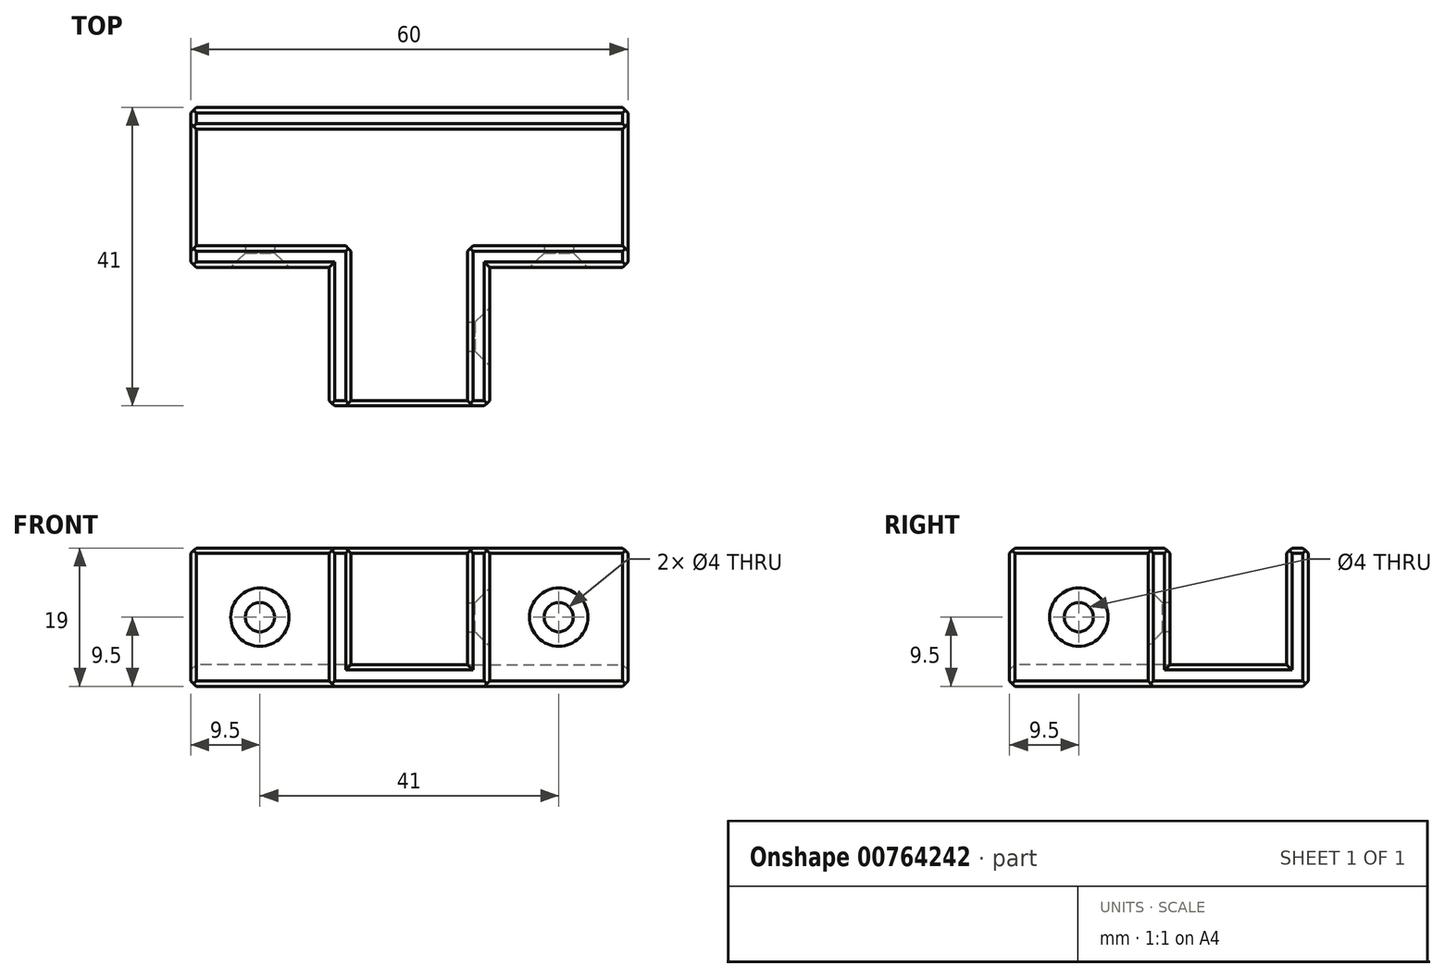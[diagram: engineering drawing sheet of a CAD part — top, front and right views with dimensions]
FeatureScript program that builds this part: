
annotation { "Feature Type Name" : "Feature", "Feature Type Description" : "" }
export const myFeature = defineFeature(function(context is Context, id is Id, definition is map)
    precondition{}
    {
        {
            var Q0;
            Q0=qCreatedBy(makeId("Top.planeOp"),FACE);
            var sketch = newSketch(context, id + "F0", { "sketchPlane" : qUnion([Q0])});
            skLineSegment(sketch, "E0.bottom", {"start": v(0, 0) * mm, "end": v(60, 0) * mm});
            skLineSegment(sketch, "E0.top", {"start": v(0, 22) * mm, "end": v(60, 22) * mm});
            skLineSegment(sketch, "E0.left", {"start": v(0, 0) * mm, "end": v(0, 22) * mm});
            skLineSegment(sketch, "E0.right", {"start": v(60, 0) * mm, "end": v(60, 22) * mm});
            skLineSegment(sketch, "E1", {"start": v(0, 0) * mm, "end": v(19, 0) * mm});
            skLineSegment(sketch, "E2.bottom", {"start": v(19, 0) * mm, "end": v(41, 0) * mm});
            skLineSegment(sketch, "E2.top", {"start": v(19, -19) * mm, "end": v(41, -19) * mm});
            skLineSegment(sketch, "E2.left", {"start": v(19, 0) * mm, "end": v(19, -19) * mm});
            skLineSegment(sketch, "E2.right", {"start": v(41, 0) * mm, "end": v(41, -19) * mm});
            skSolve(sketch);
        }
        {
            var Q0;
            Q0 = qSketchRegion(id + "F0", true);
            extrude(context, id + "F1", {"entities" : qUnion([Q0]), "depth" : 3 * mm, "offsetDistance" : 25 * mm});
        }
        {
            var Q0;
            Q0=makeQuery(id+"F1.opExtrude","CAP_FACE",FACE,{"disambiguationData":[OSD([sQuery(id+"F0.wireOp",EDGE,"E0.bottom"),sQuery(id+"F0.wireOp",EDGE,"E0.top"),sQuery(id+"F0.wireOp",EDGE,"E0.left"),sQuery(id+"F0.wireOp",EDGE,"E0.right"),sQuery(id+"F0.wireOp",EDGE,"E1"),sQuery(id+"F0.wireOp",EDGE,"E2.top"),sQuery(id+"F0.wireOp",EDGE,"E2.left"),sQuery(id+"F0.wireOp",EDGE,"E2.right")])],"isStart":false});
            var sketch = newSketch(context, id + "F2", { "sketchPlane" : qUnion([Q0])});
            skLineSegment(sketch, "E3.bottom", {"start": v(0, 22) * mm, "end": v(60, 22) * mm});
            skLineSegment(sketch, "E3.top", {"start": v(0, 19) * mm, "end": v(60, 19) * mm});
            skLineSegment(sketch, "E3.left", {"start": v(0, 22) * mm, "end": v(0, 19) * mm});
            skLineSegment(sketch, "E3.right", {"start": v(60, 22) * mm, "end": v(60, 19) * mm});
            skLineSegment(sketch, "E4.bottom", {"start": v(19, 0) * mm, "end": v(22, 0) * mm});
            skLineSegment(sketch, "E4.top", {"start": v(19, -19) * mm, "end": v(22, -19) * mm});
            skLineSegment(sketch, "E4.left", {"start": v(19, 0) * mm, "end": v(19, -19) * mm});
            skLineSegment(sketch, "E4.right", {"start": v(22, 0) * mm, "end": v(22, -19) * mm});
            skLineSegment(sketch, "E5.bottom", {"start": v(41, 0) * mm, "end": v(38, 0) * mm});
            skLineSegment(sketch, "E5.top", {"start": v(41, -19) * mm, "end": v(38, -19) * mm});
            skLineSegment(sketch, "E5.left", {"start": v(41, 0) * mm, "end": v(41, -19) * mm});
            skLineSegment(sketch, "E5.right", {"start": v(38, 0) * mm, "end": v(38, -19) * mm});
            skLineSegment(sketch, "E6.bottom", {"start": v(22, 0) * mm, "end": v(0, 0) * mm});
            skLineSegment(sketch, "E6.top", {"start": v(22, 3) * mm, "end": v(0, 3) * mm});
            skLineSegment(sketch, "E6.left", {"start": v(22, 0) * mm, "end": v(22, 3) * mm});
            skLineSegment(sketch, "E6.right", {"start": v(0, 0) * mm, "end": v(0, 3) * mm});
            skLineSegment(sketch, "E7.bottom", {"start": v(38, 0) * mm, "end": v(60, 0) * mm});
            skLineSegment(sketch, "E7.top", {"start": v(38, 3) * mm, "end": v(60, 3) * mm});
            skLineSegment(sketch, "E7.left", {"start": v(38, 0) * mm, "end": v(38, 3) * mm});
            skLineSegment(sketch, "E7.right", {"start": v(60, 0) * mm, "end": v(60, 3) * mm});
            skSolve(sketch);
        }
        {
            var Q0;
            Q0 = qSketchRegion(id + "F2", true);
            extrude(context, id + "F3", {"entities" : qUnion([Q0]), "operationType" : NewBodyOperationType.ADD, "depth" : 16 * mm, "offsetDistance" : 25 * mm});
        }
        {
            var Q0;
            Q0=makeQuery(id+"F3.boolean.opBoolean","MERGE",FACE,{"derivedFrom":[makeQuery(id+"F1.opExtrude","SWEPT_FACE",FACE,{"disambiguationData":[OSD([sQuery(id+"F0.wireOp",EDGE,"E0.bottom")])]}),makeQuery(id+"F3.opExtrude","SWEPT_FACE",FACE,{"disambiguationData":[OSD([sQuery(id+"F2.wireOp",EDGE,"E7.bottom")])]})]});
            var sketch = newSketch(context, id + "F4", { "sketchPlane" : qUnion([Q0])});
            skLineSegment(sketch, "E8", {"start": v(41, 0) * mm, "end": v(60, 19) * mm});
            skLineSegment(sketch, "E9", {"start": v(60, 19) * mm, "end": v(41, 19) * mm});
            skLineSegment(sketch, "E10", {"start": v(41, 19) * mm, "end": v(60, 0) * mm});
            skPoint(sketch, "E11", {"position": v(50.5, 9.5) * mm});
            skSolve(sketch);
        }
        {
            var Q0;
            Q0=sQuery(id+"F4.wireOp",VERTEX,"E11");
            var Q1;
            Q1=makeQuery(id+"F1.opExtrude","SWEPT_BODY",BODY,{"disambiguationData":[OSD([sQuery(id+"F0.wireOp",EDGE,"E0.bottom"),sQuery(id+"F0.wireOp",EDGE,"E0.top"),sQuery(id+"F0.wireOp",EDGE,"E0.left"),sQuery(id+"F0.wireOp",EDGE,"E0.right"),sQuery(id+"F0.wireOp",EDGE,"E1"),sQuery(id+"F0.wireOp",EDGE,"E2.top"),sQuery(id+"F0.wireOp",EDGE,"E2.left"),sQuery(id+"F0.wireOp",EDGE,"E2.right")])]});
            hole(context, id + "F5", {"style" : HoleStyle.C_SINK, "endStyle" : HoleEndStyle.BLIND, "holeDiameter" : 4 * mm, "cSinkDiameter" : 8 * mm, "cSinkAngle" : 90 * degree, "majorDiameter" : 5 * mm, "holeDepth" : 12 * mm, "isTappedThrough" : true, "tappedDepth" : 12 * mm, "tapClearance" : 3, "locations" : qUnion([Q0]), "scope" : qUnion([Q1])});
        }
        {
            var Q0;
            Q0=makeQuery(id+"F3.boolean.opBoolean","MERGE",FACE,{"derivedFrom":[makeQuery(id+"F1.opExtrude","SWEPT_FACE",FACE,{"disambiguationData":[OSD([sQuery(id+"F0.wireOp",EDGE,"E2.right")])]}),makeQuery(id+"F3.opExtrude","SWEPT_FACE",FACE,{"disambiguationData":[OSD([sQuery(id+"F2.wireOp",EDGE,"E5.left")])]})]});
            var sketch = newSketch(context, id + "F6", { "sketchPlane" : qUnion([Q0])});
            skLineSegment(sketch, "E12", {"start": v(0, 19) * mm, "end": v(-19, 0) * mm});
            skLineSegment(sketch, "E13", {"start": v(-19, 0) * mm, "end": v(-19, 19) * mm});
            skLineSegment(sketch, "E14", {"start": v(-19, 19) * mm, "end": v(0, 0) * mm});
            skPoint(sketch, "E15", {"position": v(-9.5, 9.5) * mm});
            skSolve(sketch);
        }
        {
            var Q0;
            Q0=sQuery(id+"F6.wireOp",VERTEX,"E15");
            var Q1;
            Q1=makeQuery(id+"F1.opExtrude","SWEPT_BODY",BODY,{"disambiguationData":[OSD([sQuery(id+"F0.wireOp",EDGE,"E0.bottom"),sQuery(id+"F0.wireOp",EDGE,"E0.top"),sQuery(id+"F0.wireOp",EDGE,"E0.left"),sQuery(id+"F0.wireOp",EDGE,"E0.right"),sQuery(id+"F0.wireOp",EDGE,"E1"),sQuery(id+"F0.wireOp",EDGE,"E2.top"),sQuery(id+"F0.wireOp",EDGE,"E2.left"),sQuery(id+"F0.wireOp",EDGE,"E2.right")])]});
            hole(context, id + "F7", {"style" : HoleStyle.C_SINK, "endStyle" : HoleEndStyle.BLIND, "holeDiameter" : 4 * mm, "cSinkDiameter" : 8 * mm, "cSinkAngle" : 90 * degree, "majorDiameter" : 5 * mm, "holeDepth" : 12 * mm, "isTappedThrough" : true, "tappedDepth" : 12 * mm, "tapClearance" : 3, "locations" : qUnion([Q0]), "scope" : qUnion([Q1])});
        }
        {
            var Q0;
            Q0=makeQuery(id+"F3.boolean.opBoolean","MERGE",FACE,{"derivedFrom":[makeQuery(id+"F1.opExtrude","SWEPT_FACE",FACE,{"disambiguationData":[OSD([sQuery(id+"F0.wireOp",EDGE,"E1")])]}),makeQuery(id+"F3.opExtrude","SWEPT_FACE",FACE,{"disambiguationData":[OSD([sQuery(id+"F2.wireOp",EDGE,"E6.bottom")])]})]});
            var sketch = newSketch(context, id + "F8", { "sketchPlane" : qUnion([Q0])});
            skLineSegment(sketch, "E16", {"start": v(0, 19) * mm, "end": v(19, 0) * mm});
            skLineSegment(sketch, "E17", {"start": v(19, 0) * mm, "end": v(19, 19) * mm});
            skLineSegment(sketch, "E18", {"start": v(19, 19) * mm, "end": v(0, 0) * mm});
            skPoint(sketch, "E19", {"position": v(9.5, 9.5) * mm});
            skSolve(sketch);
        }
        {
            var Q0;
            Q0=sQuery(id+"F8.wireOp",VERTEX,"E19");
            var Q1;
            Q1=makeQuery(id+"F1.opExtrude","SWEPT_BODY",BODY,{"disambiguationData":[OSD([sQuery(id+"F0.wireOp",EDGE,"E0.bottom"),sQuery(id+"F0.wireOp",EDGE,"E0.top"),sQuery(id+"F0.wireOp",EDGE,"E0.left"),sQuery(id+"F0.wireOp",EDGE,"E0.right"),sQuery(id+"F0.wireOp",EDGE,"E1"),sQuery(id+"F0.wireOp",EDGE,"E2.top"),sQuery(id+"F0.wireOp",EDGE,"E2.left"),sQuery(id+"F0.wireOp",EDGE,"E2.right")])]});
            hole(context, id + "F9", {"style" : HoleStyle.C_SINK, "endStyle" : HoleEndStyle.BLIND, "holeDiameter" : 4 * mm, "cSinkDiameter" : 8 * mm, "cSinkAngle" : 90 * degree, "majorDiameter" : 5 * mm, "holeDepth" : 12 * mm, "isTappedThrough" : true, "tappedDepth" : 12 * mm, "tapClearance" : 3, "locations" : qUnion([Q0]), "scope" : qUnion([Q1])});
        }
        {
            var Q0;
            Q0=makeQuery(id+"F3.boolean.opBoolean","MERGE",FACE,{"derivedFrom":[makeQuery(id+"F1.opExtrude","SWEPT_FACE",FACE,{"disambiguationData":[OSD([sQuery(id+"F0.wireOp",EDGE,"E0.right")])]}),makeQuery(id+"F3.opExtrude","SWEPT_FACE",FACE,{"disambiguationData":[OSD([sQuery(id+"F2.wireOp",EDGE,"E3.right")])]}),makeQuery(id+"F3.opExtrude","SWEPT_FACE",FACE,{"disambiguationData":[OSD([sQuery(id+"F2.wireOp",EDGE,"E7.right")])]})]});
            var Q1;
            Q1=makeQuery(id+"F3.boolean.opBoolean","MERGE",FACE,{"derivedFrom":[makeQuery(id+"F1.opExtrude","SWEPT_FACE",FACE,{"disambiguationData":[OSD([sQuery(id+"F0.wireOp",EDGE,"E2.top")])]}),makeQuery(id+"F3.opExtrude","SWEPT_FACE",FACE,{"disambiguationData":[OSD([sQuery(id+"F2.wireOp",EDGE,"E4.top")])]}),makeQuery(id+"F3.opExtrude","SWEPT_FACE",FACE,{"disambiguationData":[OSD([sQuery(id+"F2.wireOp",EDGE,"E5.top")])]})]});
            var Q2;
            Q2=makeQuery(id+"F3.boolean.opBoolean","MERGE",FACE,{"derivedFrom":[makeQuery(id+"F1.opExtrude","SWEPT_FACE",FACE,{"disambiguationData":[OSD([sQuery(id+"F0.wireOp",EDGE,"E0.left")])]}),makeQuery(id+"F3.opExtrude","SWEPT_FACE",FACE,{"disambiguationData":[OSD([sQuery(id+"F2.wireOp",EDGE,"E3.left")])]}),makeQuery(id+"F3.opExtrude","SWEPT_FACE",FACE,{"disambiguationData":[OSD([sQuery(id+"F2.wireOp",EDGE,"E6.right")])]})]});
            chamfer(context, id + "F10", {"entities" : qUnion([Q0, Q1, Q2]), "width" : 0.75 * mm, "tangentPropagation" : true});
        }
        {
            var Q0;
            Q0=makeQuery(id+"F3.opExtrude","SWEPT_EDGE",EDGE,{"disambiguationData":[OSD([sQuery(id+"F2.wireOp",EDGE,"E7.top"),sQuery(id+"F2.wireOp",EDGE,"E7.left")])]});
            var Q1;
            Q1=makeQuery(id+"F3.opExtrude","SWEPT_EDGE",EDGE,{"disambiguationData":[OSD([sQuery(id+"F2.wireOp",EDGE,"E6.top"),sQuery(id+"F2.wireOp",EDGE,"E6.left")])]});
            chamfer(context, id + "F11", {"entities" : qUnion([Q0, Q1]), "width" : 0.75 * mm, "tangentPropagation" : true});
        }
        {
            var Q0;
            Q0=makeQuery(id+"F3.opExtrude","CAP_EDGE",EDGE,{"disambiguationData":[OSD([sQuery(id+"F2.wireOp",EDGE,"E3.bottom")])],"isStart":false});
            var Q1;
            Q1=makeQuery(id+"F3.opExtrude","CAP_EDGE",EDGE,{"disambiguationData":[OSD([sQuery(id+"F2.wireOp",EDGE,"E3.top")])],"isStart":false});
            var Q2;
            Q2=makeQuery(id+"F3.opExtrude","CAP_EDGE",EDGE,{"disambiguationData":[OSD([sQuery(id+"F2.wireOp",EDGE,"E7.top")])],"isStart":false});
            var Q3;
            Q3=makeQuery(id+"F3.opExtrude","CAP_EDGE",EDGE,{"disambiguationData":[OSD([sQuery(id+"F2.wireOp",EDGE,"E7.bottom")])],"isStart":false});
            var Q4;
            Q4=makeQuery(id+"F3.opExtrude","CAP_EDGE",EDGE,{"disambiguationData":[OSD([sQuery(id+"F2.wireOp",EDGE,"E5.left")])],"isStart":false});
            var Q5;
            Q5=makeQuery(id+"F3.opExtrude","CAP_EDGE",EDGE,{"disambiguationData":[OSD([sQuery(id+"F2.wireOp",EDGE,"E5.right"),sQuery(id+"F2.wireOp",EDGE,"E7.left")])],"isStart":false});
            var Q6;
            Q6=makeQuery(id+"F3.opExtrude","CAP_EDGE",EDGE,{"disambiguationData":[OSD([sQuery(id+"F2.wireOp",EDGE,"E4.right"),sQuery(id+"F2.wireOp",EDGE,"E6.left")])],"isStart":false});
            var Q7;
            Q7=makeQuery(id+"F3.opExtrude","CAP_EDGE",EDGE,{"disambiguationData":[OSD([sQuery(id+"F2.wireOp",EDGE,"E4.left")])],"isStart":false});
            var Q8;
            Q8=makeQuery(id+"F3.opExtrude","CAP_EDGE",EDGE,{"disambiguationData":[OSD([sQuery(id+"F2.wireOp",EDGE,"E6.top")])],"isStart":false});
            var Q9;
            Q9=makeQuery(id+"F3.opExtrude","CAP_EDGE",EDGE,{"disambiguationData":[OSD([sQuery(id+"F2.wireOp",EDGE,"E6.bottom")])],"isStart":false});
            chamfer(context, id + "F12", {"entities" : qUnion([Q0, Q1, Q2, Q3, Q4, Q5, Q6, Q7, Q8, Q9]), "width" : 0.75 * mm, "tangentPropagation" : true});
        }
        {
            var Q0;
            Q0=makeQuery(id+"F1.opExtrude","CAP_EDGE",EDGE,{"disambiguationData":[OSD([sQuery(id+"F0.wireOp",EDGE,"E1")])],"isStart":true});
            var Q1;
            Q1=makeQuery(id+"F1.opExtrude","CAP_EDGE",EDGE,{"disambiguationData":[OSD([sQuery(id+"F0.wireOp",EDGE,"E2.left")])],"isStart":true});
            var Q2;
            Q2=makeQuery(id+"F1.opExtrude","CAP_EDGE",EDGE,{"disambiguationData":[OSD([sQuery(id+"F0.wireOp",EDGE,"E2.right")])],"isStart":true});
            var Q3;
            Q3=makeQuery(id+"F1.opExtrude","CAP_EDGE",EDGE,{"disambiguationData":[OSD([sQuery(id+"F0.wireOp",EDGE,"E0.bottom")])],"isStart":true});
            var Q4;
            Q4=makeQuery(id+"F1.opExtrude","CAP_EDGE",EDGE,{"disambiguationData":[OSD([sQuery(id+"F0.wireOp",EDGE,"E0.top")])],"isStart":true});
            chamfer(context, id + "F13", {"entities" : qUnion([Q0, Q1, Q2, Q3, Q4]), "width" : 0.75 * mm, "tangentPropagation" : true});
        }
    });
